# Revit family: P560263-031
name_source: partatom
category: Lighting Fixtures
units: mm (PartAtom-declared; Revit-internal decimal feet)

## family parameters
Cut with Voids When Loaded = No
Host = Face
Light Source = Yes
OmniClass Number = 23.80.70.11.14.11
OmniClass Title = Downlights
Part Type = Normal
Room Calculation Point = No
Round Connector Dimension = Use Diameter
Shared = No

## types (1)
- P560263-031
    Apparent Load = 25 VA
    Ballast = Paint - Hubbell - Carbon Black
    Certifications = • cCSAus certified to UL 1598
• Wall Mount: Suitable for wet locations
• Surface & Pendant Mount: Suitable for wet
locations under covered ceiling
• Cord Mount and all Wall Wash: Suitable for
damp locations
    Color Filter = 16777215
    Default Elevation = 48 "
    Description = Tremont Collection 1-Light Clear Seeded Glass Matte Black Industrial Outdoor Medium Wall Lantern Light
    Dimming Lamp Color Temperature Shift = <None>
    Features = Application: Ideal for any porch, patio, deck, garage, barn, entryway, foyer, or bedroom.
Style: Perfect for coastal, farmhouse, and urban industrial style settings.
Finish: The wall light's round backplate, curved arm, and round shade decorated with mechanical stainless-steel fittings are coated in a matte black finish to accentuate the design's industrial aesthetic.
Materials: Constructed from steel to ensure a long product lifespan.
Glass/Shade: A light source glows from within a clear seeded glass shade reminiscent of raindrops on a window after a summer thunderstorm for a touch of rustic character.
Bulbs: For ideal illumination, use 1 medium base bulb that is sold separately (60w max - LED/CFL/incandescent). Compatible with dimmable bulbs.
Dimensions: Measures 9-inch length by 11-inch height by 10-inch depth (extends from wall).
Certifications: cCSAus wet location listed.
Pairs With: Pairs with a variety of Progress Lighting fixtures from other collections.
Warranty: Our 1-Year Limited Warranty guarantees your complete satisfaction with your purchase and includes professional after-sales customer service support. Make your purchase today to breathe new life into your lighting design!
    Glass = Paint - Hubbell - White Texture
    Gold = Hubbell - Gold
    Housing Material = Paint - Hubbell - Textured Camera Black
    Lamp = LED/CFL/incandescent
    Manufacturer = Progress Lighting
    Model = P560263-031
    Photometric Web File = generic.ies
    Product Documentation Link = https://hubbellcdn.com
    Product Page URL = https://www.hubbell.com
    Reflector = Glass - Hubbell - Glass
    Tilt Angle = -90.00°
    URL = https://www.hubbell.com
    Voltage = 120 V
    Warranty = 1 year warranty
    Wattage Comments = 60W

## geometry (parser evidence)
native form markers: Blend x4, Sweep x2
no freeform markers — native parametric forms only
